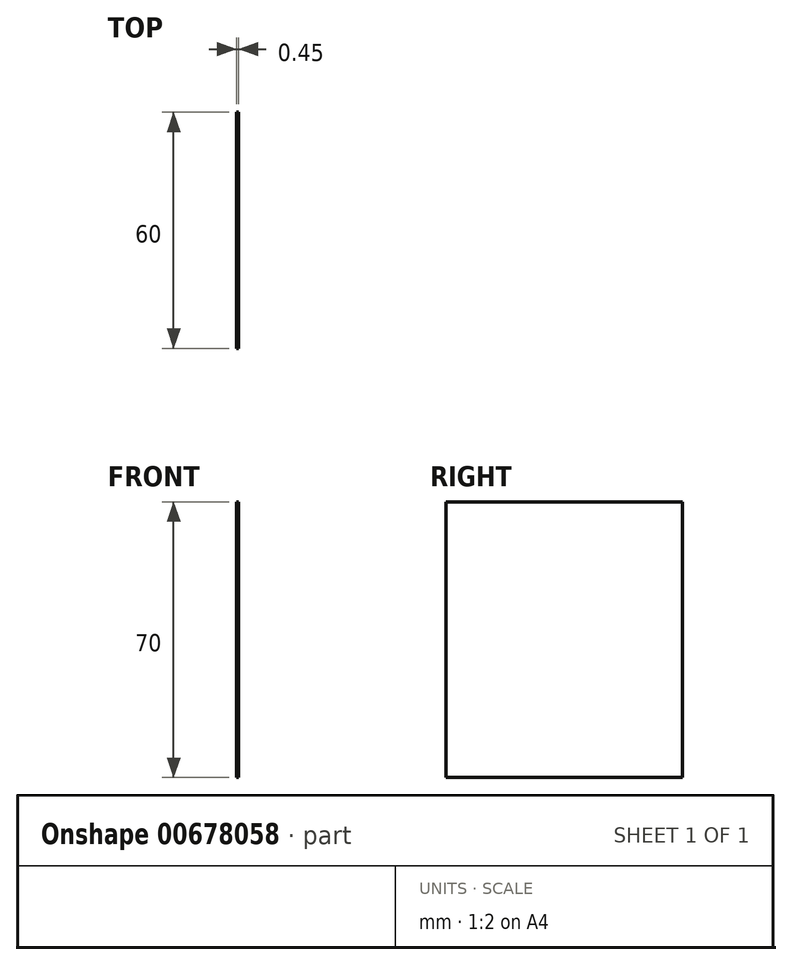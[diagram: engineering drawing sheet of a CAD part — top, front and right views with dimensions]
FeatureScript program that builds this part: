
annotation { "Feature Type Name" : "Feature", "Feature Type Description" : "" }
export const myFeature = defineFeature(function(context is Context, id is Id, definition is map)
    precondition{}
    {
        {
            var Q0;
            Q0=qCreatedBy(makeId("Right.planeOp"),FACE);
            var sketch = newSketch(context, id + "F0", { "sketchPlane" : qUnion([Q0])});
            skLineSegment(sketch, "E0.bottom", {"start": v(0, 0) * mm, "end": v(60, 0) * mm});
            skLineSegment(sketch, "E0.top", {"start": v(0, -70) * mm, "end": v(60, -70) * mm});
            skLineSegment(sketch, "E0.left", {"start": v(0, 0) * mm, "end": v(0, -70) * mm});
            skLineSegment(sketch, "E0.right", {"start": v(60, 0) * mm, "end": v(60, -70) * mm});
            skSolve(sketch);
        }
        {
            var Q0;
            Q0=makeQuery(id+"F0.imprint","IMPRINT",FACE,{"disambiguationData":[TD([[makeQuery(id+"F0.imprint","IMPRINT",EDGE,{"derivedFrom":sQuery(id+"F0.wireOp",EDGE,"E0.bottom")}),-1.0]])]});
            extrude(context, id + "F1", {"entities" : qUnion([Q0]), "depth" : .45 * mm, "offsetDistance" : 25 * mm});
        }
    });
